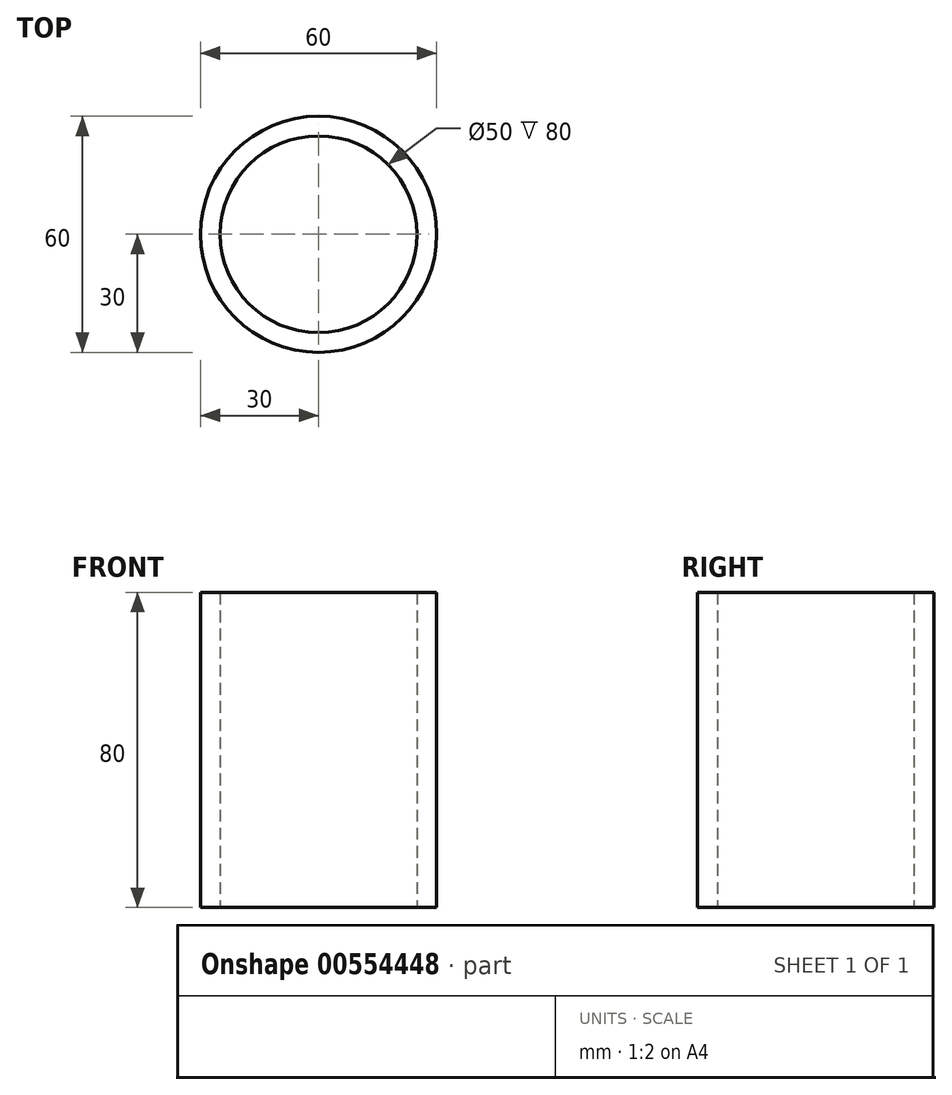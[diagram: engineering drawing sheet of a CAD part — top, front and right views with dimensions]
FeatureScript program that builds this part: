
annotation { "Feature Type Name" : "Feature", "Feature Type Description" : "" }
export const myFeature = defineFeature(function(context is Context, id is Id, definition is map)
    precondition{}
    {
        {
            var Q0;
            Q0=qCreatedBy(makeId("Top.planeOp"),FACE);
            var sketch = newSketch(context, id + "F0", { "sketchPlane" : qUnion([Q0])});
            skCircle(sketch, "E0", {"center": v(0, 0) * mm, "radius": 30 * mm});
            skCircle(sketch, "E1", {"center": v(0, 0) * mm, "radius": 25 * mm});
            skSolve(sketch);
        }
        {
            var Q0;
            Q0=makeQuery(id+"F0.imprint","IMPRINT",FACE,{"disambiguationData":[TD([[makeQuery(id+"F0.imprint","IMPRINT",EDGE,{"derivedFrom":sQuery(id+"F0.wireOp",EDGE,"E0")}),1.0]])]});
            extrude(context, id + "F1", {"entities" : qUnion([Q0]), "depth" : 80 * mm, "offsetDistance" : 25 * mm});
        }
    });
